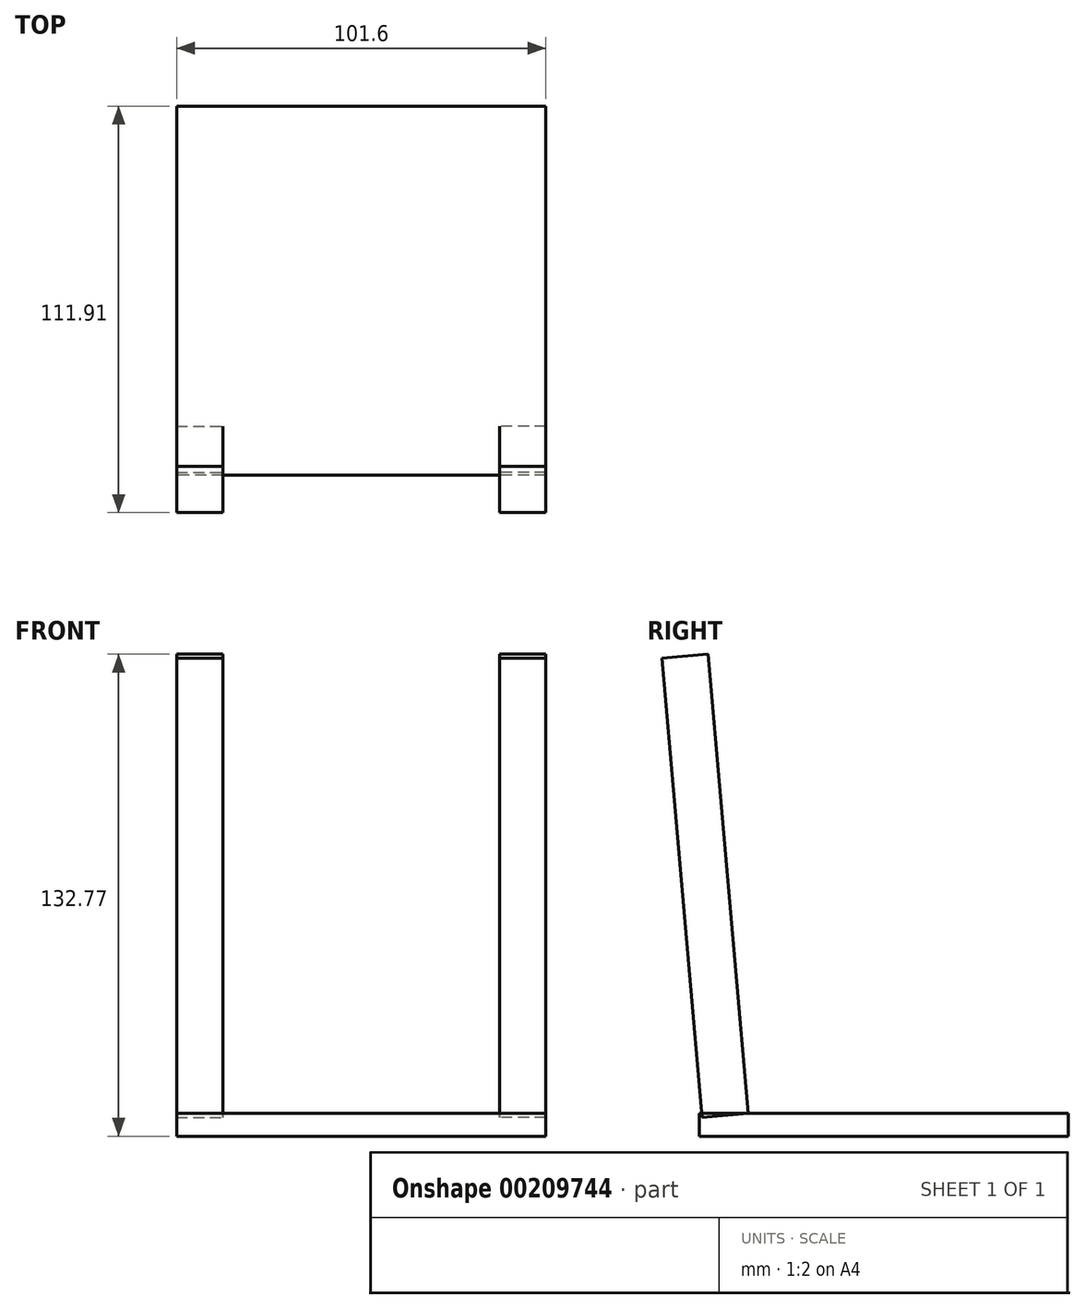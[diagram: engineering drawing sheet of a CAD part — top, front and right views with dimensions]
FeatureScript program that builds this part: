
annotation { "Feature Type Name" : "Feature", "Feature Type Description" : "" }
export const myFeature = defineFeature(function(context is Context, id is Id, definition is map)
    precondition{}
    {
        {
            var Q0;
            Q0=qCreatedBy(makeId("Top.planeOp"),FACE);
            var sketch = newSketch(context, id + "F0", { "sketchPlane" : qUnion([Q0])});
            skLineSegment(sketch, "E0.bottom", {"start": v(50.8, 50.8) * mm, "end": v(-50.8, 50.8) * mm});
            skLineSegment(sketch, "E0.top", {"start": v(50.8, -50.8) * mm, "end": v(-50.8, -50.8) * mm});
            skLineSegment(sketch, "E0.left", {"start": v(50.8, 50.8) * mm, "end": v(50.8, -50.8) * mm});
            skLineSegment(sketch, "E0.right", {"start": v(-50.8, 50.8) * mm, "end": v(-50.8, -50.8) * mm});
            skPoint(sketch, "E0.middle", {"position": v(0, 0) * mm});
            skSolve(sketch);
        }
        {
            var Q0;
            Q0=makeQuery(id+"F0.imprint","IMPRINT",FACE,{"disambiguationData":[TD([[makeQuery(id+"F0.imprint","IMPRINT",EDGE,{"derivedFrom":sQuery(id+"F0.wireOp",EDGE,"E0.bottom")}),1.0]])]});
            extrude(context, id + "F1", {"entities" : qUnion([Q0]), "depth" : 6.35 * mm});
        }
        {
            var Q0;
            Q0=makeQuery(id+"F1.opExtrude","SWEPT_FACE",FACE,{"disambiguationData":[OSD([sQuery(id+"F0.wireOp",EDGE,"E0.top")])]});
            var sketch = newSketch(context, id + "F2", { "sketchPlane" : qUnion([Q0])});
            skLineSegment(sketch, "E1", {"start": v(50.8, 5.08) * mm, "end": v(-50.8, 5.08) * mm});
            skSolve(sketch);
        }
        {
            var Q0;
            Q0=sQuery(id+"F2.wireOp",EDGE,"E1");
            cPlane(context, id + "F3", {"entities" : qUnion([Q0]), "cplaneType" : CPlaneType.LINE_ANGLE, "offset" : 25.4 * mm, "angle" : 85 * degree, "width" : 152.4 * mm, "height" : 152.4 * mm});
        }
        {
            var Q0;
            Q0=qCreatedBy(id+"F3.planeOp",FACE);
            var sketch = newSketch(context, id + "F4", { "sketchPlane" : qUnion([Q0])});
            skLineSegment(sketch, "E2.bottom", {"start": v(-50.8, -49.4) * mm, "end": v(-38.1, -49.4) * mm});
            skLineSegment(sketch, "E2.top", {"start": v(-50.8, -36.7) * mm, "end": v(-38.1, -36.7) * mm});
            skLineSegment(sketch, "E2.left", {"start": v(-50.8, -49.4) * mm, "end": v(-50.8, -36.7) * mm});
            skLineSegment(sketch, "E2.right", {"start": v(-38.1, -49.4) * mm, "end": v(-38.1, -36.7) * mm});
            skLineSegment(sketch, "E3.bottom", {"start": v(50.8, -49.4) * mm, "end": v(38.1, -49.4) * mm});
            skLineSegment(sketch, "E3.top", {"start": v(50.8, -36.7) * mm, "end": v(38.1, -36.7) * mm});
            skLineSegment(sketch, "E3.left", {"start": v(50.8, -49.4) * mm, "end": v(50.8, -36.7) * mm});
            skLineSegment(sketch, "E3.right", {"start": v(38.1, -49.4) * mm, "end": v(38.1, -36.7) * mm});
            skSolve(sketch);
        }
        {
            var Q0;
            Q0 = qSketchRegion(id + "F4", true);
            var Q1;
            Q1=sQuery(id+"F4.wireOp",EDGE,"E2.left");
            var Q2;
            Q2=sQuery(id+"F4.wireOp",EDGE,"E2.top");
            var Q3;
            Q3=sQuery(id+"F4.wireOp",EDGE,"E2.right");
            var Q4;
            Q4=sQuery(id+"F4.wireOp",EDGE,"E2.bottom");
            var Q5;
            Q5=sQuery(id+"F4.wireOp",EDGE,"E3.right");
            var Q6;
            Q6=sQuery(id+"F4.wireOp",EDGE,"E3.top");
            var Q7;
            Q7=sQuery(id+"F4.wireOp",EDGE,"E3.bottom");
            var Q8;
            Q8=sQuery(id+"F4.wireOp",EDGE,"E3.left");
            extrude(context, id + "F5", {"entities" : qUnion([Q0]), "surfaceEntities" : qUnion([Q1, Q2, Q3, Q4, Q5, Q6, Q7, Q8]), "depth" : 127 * mm});
        }
    });
